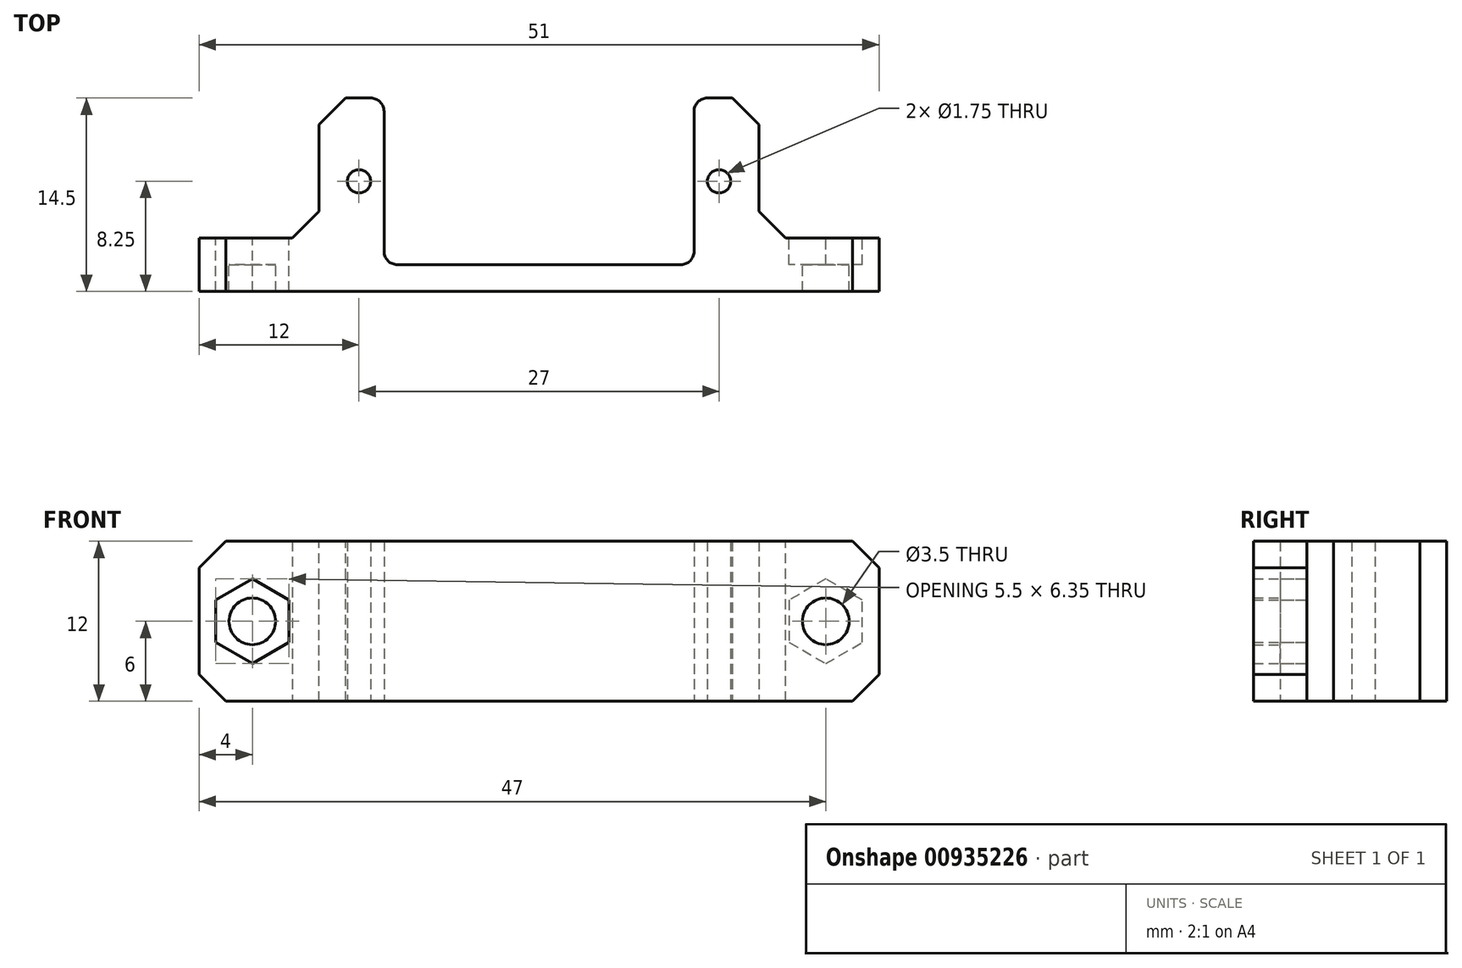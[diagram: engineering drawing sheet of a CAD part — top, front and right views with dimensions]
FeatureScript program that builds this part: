
annotation { "Feature Type Name" : "Feature", "Feature Type Description" : "" }
export const myFeature = defineFeature(function(context is Context, id is Id, definition is map)
    precondition{}
    {
        {
            var Q0;
            Q0=qCreatedBy(makeId("Top.planeOp"),FACE);
            var sketch = newSketch(context, id + "F0", { "sketchPlane" : qUnion([Q0])});
            skLineSegment(sketch, "E0.bottom", {"start": v(-16.5, 7.25) * mm, "end": v(16.5, 7.25) * mm});
            skLineSegment(sketch, "E0.top", {"start": v(-16.5, -7.25) * mm, "end": v(16.5, -7.25) * mm});
            skLineSegment(sketch, "E0.left", {"start": v(-16.5, 7.25) * mm, "end": v(-16.5, -7.25) * mm});
            skLineSegment(sketch, "E0.right", {"start": v(16.5, 7.25) * mm, "end": v(16.5, -7.25) * mm});
            skPoint(sketch, "E0.middle", {"position": v(0, 0) * mm});
            skLineSegment(sketch, "E1.bottom", {"start": v(-16.5, -3.25) * mm, "end": v(-25.5, -3.25) * mm});
            skLineSegment(sketch, "E1.top", {"start": v(-16.5, -7.25) * mm, "end": v(-25.5, -7.25) * mm});
            skLineSegment(sketch, "E1.left", {"start": v(-16.5, -3.25) * mm, "end": v(-16.5, -7.25) * mm});
            skLineSegment(sketch, "E1.right", {"start": v(-25.5, -3.25) * mm, "end": v(-25.5, -7.25) * mm});
            skLineSegment(sketch, "E2.MirrorCS", {"start": v(16.5, -3.25) * mm, "end": v(25.5, -3.25) * mm});
            skLineSegment(sketch, "E3.MirrorCS", {"start": v(16.5, -7.25) * mm, "end": v(25.5, -7.25) * mm});
            skLineSegment(sketch, "E4.MirrorCS", {"start": v(25.5, -3.25) * mm, "end": v(25.5, -7.25) * mm});
            skLineSegment(sketch, "E5.bottom", {"start": v(-11.62, 7.25) * mm, "end": v(11.62, 7.25) * mm});
            skLineSegment(sketch, "E5.top", {"start": v(-11.62, -5.25) * mm, "end": v(11.62, -5.25) * mm});
            skLineSegment(sketch, "E5.left", {"start": v(-11.62, 7.25) * mm, "end": v(-11.62, -5.25) * mm});
            skLineSegment(sketch, "E5.right", {"start": v(11.62, 7.25) * mm, "end": v(11.62, -5.25) * mm});
            skCircle(sketch, "E6", {"center": v(-13.5, 1) * mm, "radius": 0.88 * mm});
            skCircle(sketch, "E7.MirrorC", {"center": v(13.5, 1) * mm, "radius": 0.88 * mm});
            skLineSegment(sketch, "E8", {"start": v(-11.62, -5.25) * mm, "end": v(-16.5, -5.25) * mm});
            skLineSegment(sketch, "E9", {"start": v(11.62, -5.25) * mm, "end": v(16.5, -5.25) * mm});
            skSolve(sketch);
        }
        {
            var Q0;
            {var subQ1=sQuery(id+"F0.wireOp",EDGE,"E0.top");Q0=makeQuery(id+"F0.imprint","IMPRINT",FACE,{"disambiguationData":[TD([[makeQuery(id+"F0.imprint","IMPRINT",EDGE,{"derivedFrom":subQ1}),1.0]])]});}
            var Q1;
            Q1=makeQuery(id+"F0.imprint","IMPRINT",FACE,{"disambiguationData":[TD([[makeQuery(id+"F0.imprint","IMPRINT",EDGE,{"derivedFrom":sQuery(id+"F0.wireOp",EDGE,"E1.bottom")}),1.0]])]});
            var Q2;
            {var subQ2=sQuery(id+"F0.wireOp",EDGE,"E2.MirrorCS");Q2=makeQuery(id+"F0.imprint","IMPRINT",FACE,{"disambiguationData":[TD([[makeQuery(id+"F0.imprint","IMPRINT",EDGE,{"derivedFrom":subQ2}),-1.0]])]});}
            var Q3;
            {var subQ2=sQuery(id+"F0.wireOp",EDGE,"E0.left");Q3=makeQuery(id+"F0.imprint","IMPRINT",FACE,{"disambiguationData":[TD([[makeQuery(id+"F0.imprint","IMPRINT",EDGE,{"derivedFrom":subQ2}),1.0]])]});}
            var Q4;
            {var subQ0=sQuery(id+"F0.wireOp",EDGE,"E5.right");Q4=makeQuery(id+"F0.imprint","IMPRINT",FACE,{"disambiguationData":[TD([[makeQuery(id+"F0.imprint","IMPRINT",EDGE,{"derivedFrom":subQ0}),1.0]])]});}
            extrude(context, id + "F1", {"entities" : qUnion([Q0, Q1, Q2, Q3, Q4]), "depth" : 12 * mm, "offsetDistance" : 25 * mm});
        }
        {
            var Q0;
            Q0=makeQuery(id+"F1.opExtrude","SWEPT_EDGE",EDGE,{"disambiguationData":[OSD([sQuery(id+"F0.wireOp",EDGE,"E0.left"),sQuery(id+"F0.wireOp",EDGE,"E1.bottom"),sQuery(id+"F0.wireOp",EDGE,"E1.left")])]});
            var Q1;
            Q1=makeQuery(id+"F1.opExtrude","SWEPT_EDGE",EDGE,{"disambiguationData":[OSD([sQuery(id+"F0.wireOp",EDGE,"E0.right"),sQuery(id+"F0.wireOp",EDGE,"E2.MirrorCS")])]});
            var Q2;
            Q2=makeQuery(id+"F1.opExtrude","CAP_EDGE",EDGE,{"disambiguationData":[OSD([sQuery(id+"F0.wireOp",EDGE,"E4.MirrorCS")])],"isStart":false});
            var Q3;
            Q3=makeQuery(id+"F1.opExtrude","CAP_EDGE",EDGE,{"disambiguationData":[OSD([sQuery(id+"F0.wireOp",EDGE,"E4.MirrorCS")])],"isStart":true});
            var Q4;
            Q4=makeQuery(id+"F1.opExtrude","CAP_EDGE",EDGE,{"disambiguationData":[OSD([sQuery(id+"F0.wireOp",EDGE,"E1.right")])],"isStart":false});
            var Q5;
            Q5=makeQuery(id+"F1.opExtrude","CAP_EDGE",EDGE,{"disambiguationData":[OSD([sQuery(id+"F0.wireOp",EDGE,"E1.right")])],"isStart":true});
            var Q6;
            Q6=makeQuery(id+"F1.opExtrude","SWEPT_EDGE",EDGE,{"disambiguationData":[OSD([sQuery(id+"F0.wireOp",EDGE,"E0.bottom"),sQuery(id+"F0.wireOp",EDGE,"E0.right")])]});
            var Q7;
            Q7=makeQuery(id+"F1.opExtrude","SWEPT_EDGE",EDGE,{"disambiguationData":[OSD([sQuery(id+"F0.wireOp",EDGE,"E0.bottom"),sQuery(id+"F0.wireOp",EDGE,"E0.left")])]});
            chamfer(context, id + "F2", {"entities" : qUnion([Q0, Q1, Q2, Q3, Q4, Q5, Q6, Q7]), "width" : 2 * mm, "tangentPropagation" : true});
        }
        {
            var Q0;
            Q0=makeQuery(id+"F1.opExtrude","SWEPT_FACE",FACE,{"disambiguationData":[OSD([sQuery(id+"F0.wireOp",EDGE,"E1.bottom")])]});
            var sketch = newSketch(context, id + "F3", { "sketchPlane" : qUnion([Q0])});
            skCircle(sketch, "E10", {"center": v(-21.5, 6) * mm, "radius": 1.75 * mm});
            skLineSegment(sketch, "E11", {"start": v(-21.5, 6) * mm, "end": v(-25.5, 6) * mm, "construction": true});
            skLineSegment(sketch, "E12", {"start": v(-21.5, 6) * mm, "end": v(-17.5, 6) * mm, "construction": true});
            skCircle(sketch, "E13.MirrorC", {"center": v(21.5, 6) * mm, "radius": 1.75 * mm});
            skCircle(sketch, "E14.cCircle", {"center": v(-21.5, 6) * mm, "radius": 2.75 * mm, "construction": true});
            skLineSegment(sketch, "E14.0", {"start": v(-18.75, 7.59) * mm, "end": v(-18.75, 4.41) * mm});
            skLineSegment(sketch, "E14.1", {"start": v(-18.75, 4.41) * mm, "end": v(-21.5, 2.82) * mm});
            skLineSegment(sketch, "E14.2", {"start": v(-21.5, 2.82) * mm, "end": v(-24.25, 4.41) * mm});
            skLineSegment(sketch, "E14.3", {"start": v(-24.25, 4.41) * mm, "end": v(-24.25, 7.59) * mm});
            skLineSegment(sketch, "E14.4", {"start": v(-24.25, 7.59) * mm, "end": v(-21.5, 9.18) * mm});
            skLineSegment(sketch, "E14.5", {"start": v(-21.5, 9.18) * mm, "end": v(-18.75, 7.59) * mm});
            skPoint(sketch, "E14.0.midPoint", {"position": v(-18.75, 6) * mm});
            skLineSegment(sketch, "E15.MirrorCS", {"start": v(18.75, 4.41) * mm, "end": v(21.5, 2.82) * mm});
            skLineSegment(sketch, "E16.MirrorCS", {"start": v(21.5, 2.82) * mm, "end": v(24.25, 4.41) * mm});
            skLineSegment(sketch, "E17.MirrorCS", {"start": v(24.25, 4.41) * mm, "end": v(24.25, 7.59) * mm});
            skLineSegment(sketch, "E18.MirrorCS", {"start": v(24.25, 7.59) * mm, "end": v(21.5, 9.18) * mm});
            skLineSegment(sketch, "E19.MirrorCS", {"start": v(21.5, 9.18) * mm, "end": v(18.75, 7.59) * mm});
            skLineSegment(sketch, "E20.MirrorCS", {"start": v(18.75, 7.59) * mm, "end": v(18.75, 4.41) * mm});
            skSolve(sketch);
        }
        {
            var Q0;
            Q0=makeQuery(id+"F3.imprint","IMPRINT",FACE,{"disambiguationData":[TD([[makeQuery(id+"F3.imprint","IMPRINT",EDGE,{"derivedFrom":sQuery(id+"F3.wireOp",EDGE,"E13.MirrorC")}),-1.0]])]});
            var Q1;
            Q1=makeQuery(id+"F3.imprint","IMPRINT",FACE,{"disambiguationData":[TD([[makeQuery(id+"F3.imprint","IMPRINT",EDGE,{"derivedFrom":sQuery(id+"F3.wireOp",EDGE,"E10")}),1.0]])]});
            var Q2;
            Q2=makeQuery(id+"F1.opExtrude","SWEPT_FACE",FACE,{"disambiguationData":[OSD([sQuery(id+"F0.wireOp",EDGE,"E0.top"),sQuery(id+"F0.wireOp",EDGE,"E1.top"),sQuery(id+"F0.wireOp",EDGE,"E3.MirrorCS")])]});
            extrude(context, id + "F4", {"entities" : qUnion([Q0, Q1]), "operationType" : NewBodyOperationType.REMOVE, "endBound" : BoundingType.UP_TO_SURFACE, "oppositeDirection" : true, "depth" : 25 * mm, "endBoundEntityFace" : qUnion([Q2]), "offsetDistance" : 25 * mm});
        }
        {
            var Q0;
            Q0=makeQuery(id+"F3.imprint","IMPRINT",FACE,{"disambiguationData":[TD([[makeQuery(id+"F3.imprint","IMPRINT",EDGE,{"derivedFrom":sQuery(id+"F3.wireOp",EDGE,"E10")}),-1.0]])]});
            var Q1;
            Q1=makeQuery(id+"F3.imprint","IMPRINT",FACE,{"disambiguationData":[TD([[makeQuery(id+"F3.imprint","IMPRINT",EDGE,{"derivedFrom":sQuery(id+"F3.wireOp",EDGE,"E13.MirrorC")}),1.0]])]});
            extrude(context, id + "F5", {"entities" : qUnion([Q0, Q1]), "operationType" : NewBodyOperationType.REMOVE, "oppositeDirection" : true, "depth" : 2 * mm, "offsetDistance" : 25 * mm});
        }
        {
            var Q0;
            Q0=makeQuery(id+"F1.opExtrude","SWEPT_EDGE",EDGE,{"disambiguationData":[OSD([sQuery(id+"F0.wireOp",EDGE,"E5.top"),sQuery(id+"F0.wireOp",EDGE,"E5.right"),sQuery(id+"F0.wireOp",EDGE,"v9HbxVqt-2rQI-dspp-z2ZP-ibPVCHQ933eP")])]});
            var Q1;
            Q1=makeQuery(id+"F1.opExtrude","SWEPT_EDGE",EDGE,{"disambiguationData":[OSD([sQuery(id+"F0.wireOp",EDGE,"E5.top"),sQuery(id+"F0.wireOp",EDGE,"E5.left"),sQuery(id+"F0.wireOp",EDGE,"DVMDMKjG-olPc-v8IH-mmjh-vYbIOe0UTvFG")])]});
            var Q2;
            Q2=makeQuery(id+"F1.opExtrude","SWEPT_EDGE",EDGE,{"disambiguationData":[OSD([sQuery(id+"F0.wireOp",EDGE,"E0.bottom"),sQuery(id+"F0.wireOp",EDGE,"E5.bottom"),sQuery(id+"F0.wireOp",EDGE,"E5.left")])]});
            var Q3;
            Q3=makeQuery(id+"F1.opExtrude","SWEPT_EDGE",EDGE,{"disambiguationData":[OSD([sQuery(id+"F0.wireOp",EDGE,"E0.bottom"),sQuery(id+"F0.wireOp",EDGE,"E5.bottom"),sQuery(id+"F0.wireOp",EDGE,"E5.right")])]});
            var Q4;
            Q4=makeQuery(id+"Fj2hP9LWgfrMyZt_1.opExtrude","SWEPT_EDGE",EDGE,{"disambiguationData":[OSD([sQuery(id+"F0.wireOp",EDGE,"E0.bottom"),sQuery(id+"F0.wireOp",EDGE,"E5.bottom"),sQuery(id+"F0.wireOp",EDGE,"E5.left")])]});
            var Q5;
            Q5=makeQuery(id+"Fj2hP9LWgfrMyZt_1.opExtrude","SWEPT_EDGE",EDGE,{"disambiguationData":[OSD([sQuery(id+"F0.wireOp",EDGE,"E0.bottom"),sQuery(id+"F0.wireOp",EDGE,"E5.bottom"),sQuery(id+"F0.wireOp",EDGE,"E5.right")])]});
            var Q6;
            Q6=makeQuery(id+"Fj2hP9LWgfrMyZt_1.opExtrude","SWEPT_EDGE",EDGE,{"disambiguationData":[OSD([sQuery(id+"F0.wireOp",EDGE,"E5.top"),sQuery(id+"F0.wireOp",EDGE,"E5.left"),sQuery(id+"F0.wireOp",EDGE,"DVMDMKjG-olPc-v8IH-mmjh-vYbIOe0UTvFG")])]});
            var Q7;
            Q7=makeQuery(id+"Fj2hP9LWgfrMyZt_1.opExtrude","SWEPT_EDGE",EDGE,{"disambiguationData":[OSD([sQuery(id+"F0.wireOp",EDGE,"E5.top"),sQuery(id+"F0.wireOp",EDGE,"E5.right"),sQuery(id+"F0.wireOp",EDGE,"v9HbxVqt-2rQI-dspp-z2ZP-ibPVCHQ933eP")])]});
            fillet(context, id + "F6", {"entities" : qUnion([Q0, Q1, Q2, Q3, Q4, Q5, Q6, Q7]), "radius" : 1 * mm, "tangentPropagation" : true, "allowEdgeOverflow" : false});
        }
    });
